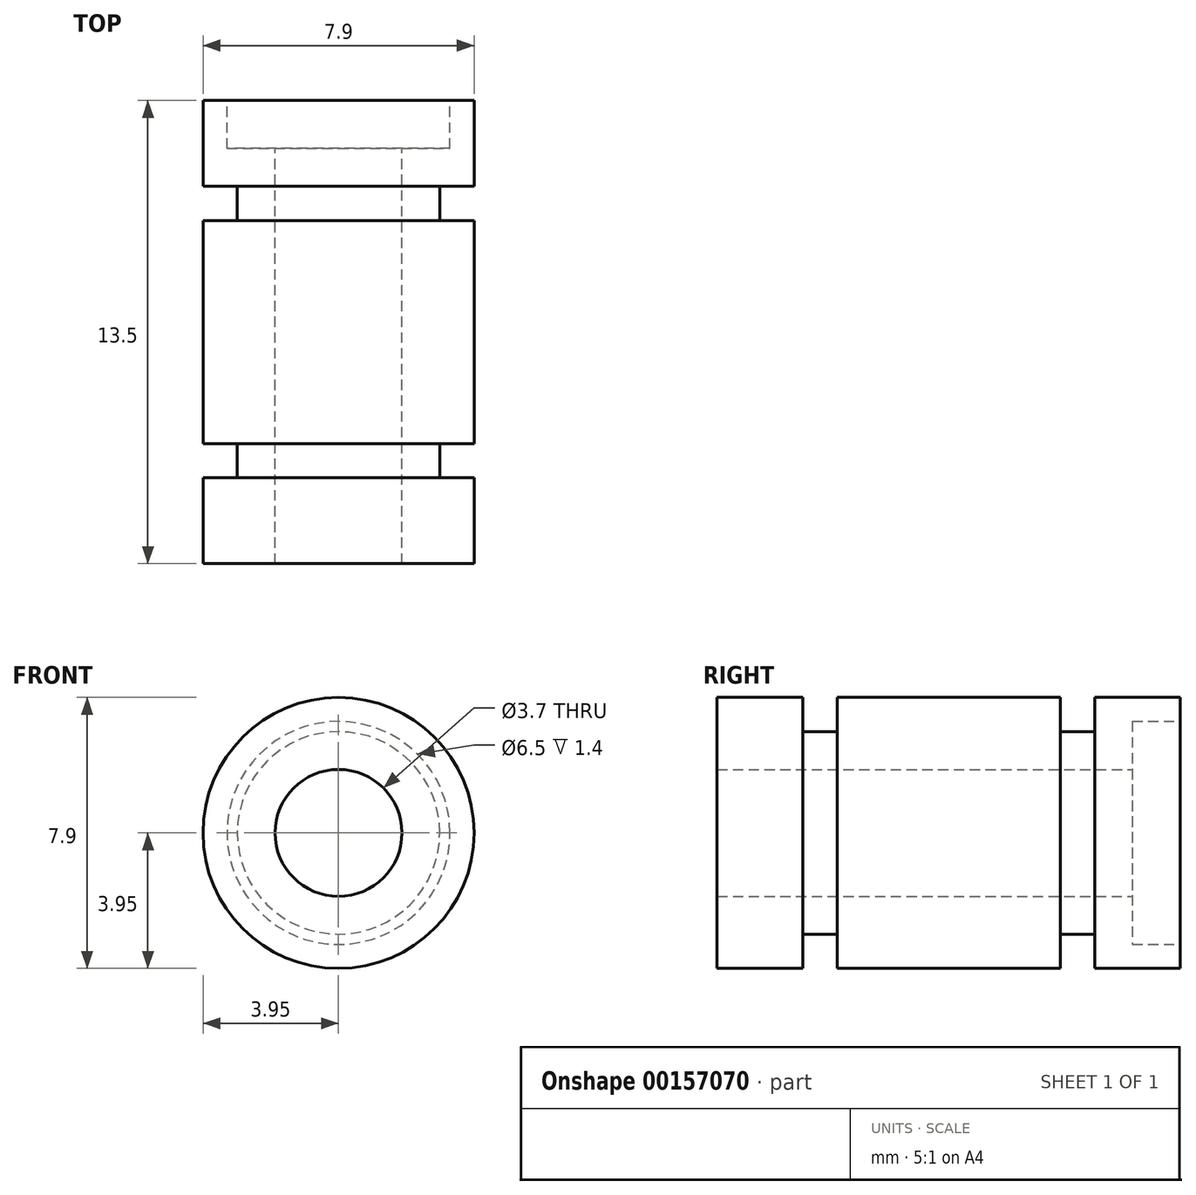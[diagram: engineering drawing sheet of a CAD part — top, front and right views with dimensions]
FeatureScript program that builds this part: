
annotation { "Feature Type Name" : "Feature", "Feature Type Description" : "" }
export const myFeature = defineFeature(function(context is Context, id is Id, definition is map)
    precondition{}
    {
        {
            var Q0;
            Q0=qCreatedBy(makeId("Right.planeOp"),FACE);
            var sketch = newSketch(context, id + "F0", { "sketchPlane" : qUnion([Q0])});
            skLineSegment(sketch, "E0", {"start": v(11.47, 0) * mm, "end": v(0, 0) * mm, "construction": true});
            skLineSegment(sketch, "E1", {"start": v(12.1, 1.85) * mm, "end": v(0, 1.85) * mm});
            skLineSegment(sketch, "E2", {"start": v(12.1, 1.85) * mm, "end": v(12.1, 3.25) * mm});
            skLineSegment(sketch, "E3", {"start": v(13.5, 3.25) * mm, "end": v(12.1, 3.25) * mm});
            skLineSegment(sketch, "E4", {"start": v(13.5, 3.25) * mm, "end": v(13.5, 3.95) * mm});
            skLineSegment(sketch, "E5", {"start": v(11, 3.95) * mm, "end": v(13.5, 3.95) * mm});
            skLineSegment(sketch, "E6", {"start": v(11, 3.95) * mm, "end": v(11, 2.95) * mm});
            skLineSegment(sketch, "E7", {"start": v(10, 2.95) * mm, "end": v(11, 2.95) * mm});
            skLineSegment(sketch, "E8", {"start": v(2.5, 2.95) * mm, "end": v(2.5, 3.95) * mm});
            skLineSegment(sketch, "E9", {"start": v(0, 3.95) * mm, "end": v(2.5, 3.95) * mm});
            skLineSegment(sketch, "E10", {"start": v(0, 3.95) * mm, "end": v(0, 1.85) * mm});
            skLineSegment(sketch, "E11", {"start": v(3.5, 2.95) * mm, "end": v(3.5, 3.95) * mm});
            skLineSegment(sketch, "E12", {"start": v(3.5, 3.95) * mm, "end": v(10, 3.95) * mm});
            skLineSegment(sketch, "E13", {"start": v(10, 3.95) * mm, "end": v(10, 2.95) * mm});
            skLineSegment(sketch, "E14.trimOffspring", {"start": v(3.5, 2.95) * mm, "end": v(2.5, 2.95) * mm});
            skSolve(sketch);
        }
        {
            var Q0;
            Q0=makeQuery(id+"F0.imprint","IMPRINT",FACE,{"disambiguationData":[TD([[makeQuery(id+"F0.imprint","IMPRINT",EDGE,{"derivedFrom":sQuery(id+"F0.wireOp",EDGE,"E1")}),-1.0]])]});
            var Q1;
            Q1=sQuery(id+"F0.wireOp",EDGE,"E0");
            revolve(context, id + "F1", {"entities" : qUnion([Q0]), "axis" : qUnion([Q1]), "revolveType" : RevolveType.FULL});
        }
    });
